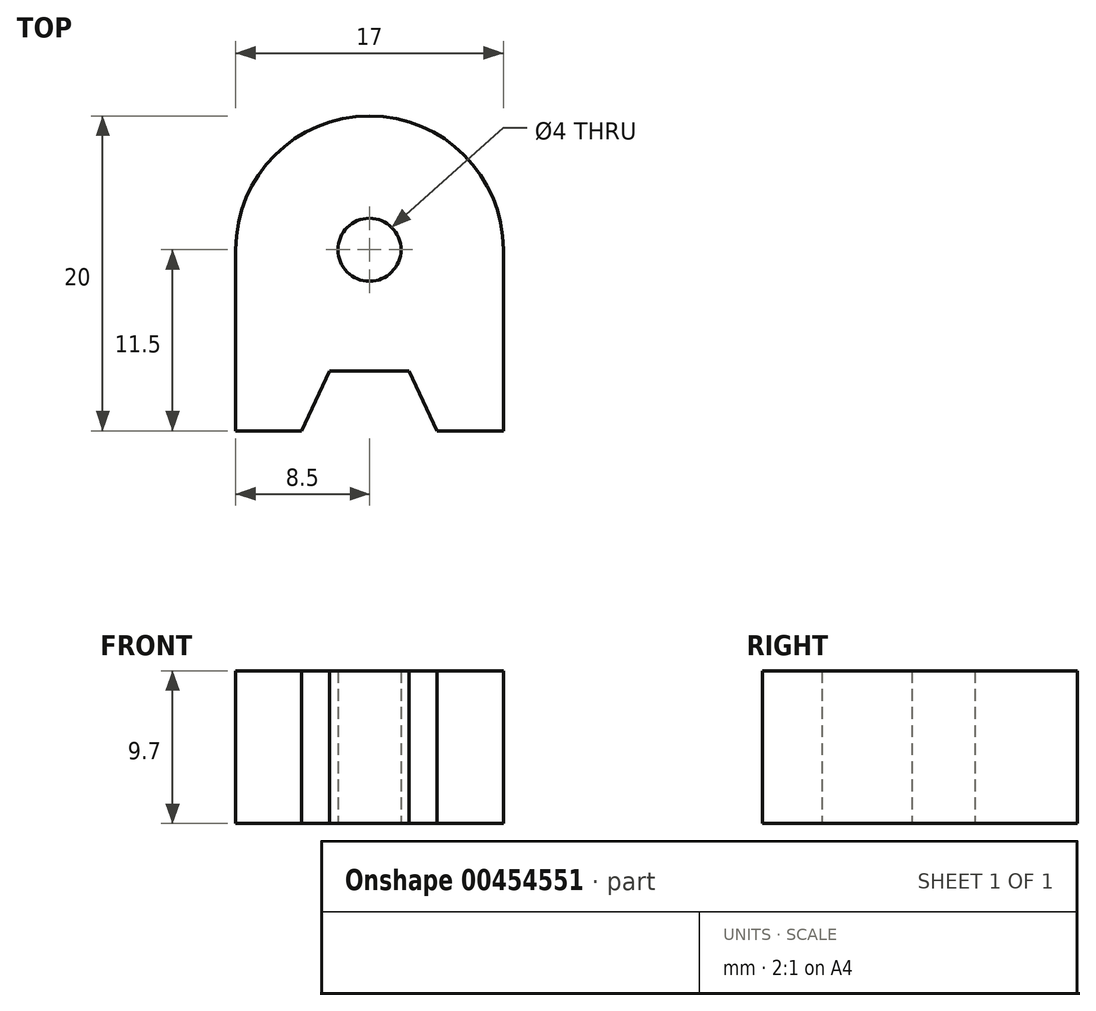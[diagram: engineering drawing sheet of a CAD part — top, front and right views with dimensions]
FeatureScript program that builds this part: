
annotation { "Feature Type Name" : "Feature", "Feature Type Description" : "" }
export const myFeature = defineFeature(function(context is Context, id is Id, definition is map)
    precondition{}
    {
        {
            var Q0;
            Q0=qCreatedBy(makeId("Top.planeOp"),FACE);
            var sketch = newSketch(context, id + "F0", { "sketchPlane" : qUnion([Q0])});
            skLineSegment(sketch, "E0", {"start": v(-8.5, 0) * mm, "end": v(-8.5, -11.5) * mm});
            skLineSegment(sketch, "E1", {"start": v(-8.5, -11.5) * mm, "end": v(-4.3, -11.5) * mm});
            skLineSegment(sketch, "E2", {"start": v(-4.3, -11.5) * mm, "end": v(-2.53, -7.7) * mm});
            skLineSegment(sketch, "E3", {"start": v(2.53, -7.7) * mm, "end": v(4.3, -11.5) * mm});
            skLineSegment(sketch, "E4", {"start": v(4.3, -11.5) * mm, "end": v(8.5, -11.5) * mm});
            skLineSegment(sketch, "E5", {"start": v(8.5, 0) * mm, "end": v(8.5, -11.5) * mm});
            skCircle(sketch, "E6", {"center": v(0, 0) * mm, "radius": 2 * mm});
            skArc(sketch, "E7", {"start": v(-8.5, 0) * mm, "mid": v(0, 8.5) * mm, "end": v(8.5, 0) * mm});
            skLineSegment(sketch, "E8", {"start": v(-2.53, -7.7) * mm, "end": v(2.53, -7.7) * mm});
            skSolve(sketch);
        }
        {
            var Q0;
            Q0 = qSketchRegion(id + "FW0XGsF4BOvdoAD_0", true);
            var Q1;
            Q1=makeQuery(id+"F0.imprint","IMPRINT",FACE,{"disambiguationData":[TD([[makeQuery(id+"F0.imprint","IMPRINT",EDGE,{"derivedFrom":sQuery(id+"F0.wireOp",EDGE,"E0")}),1.0]])]});
            extrude(context, id + "F1", {"entities" : qUnion([Q0, Q1]), "depth" : 9.7 * mm});
        }
    });
